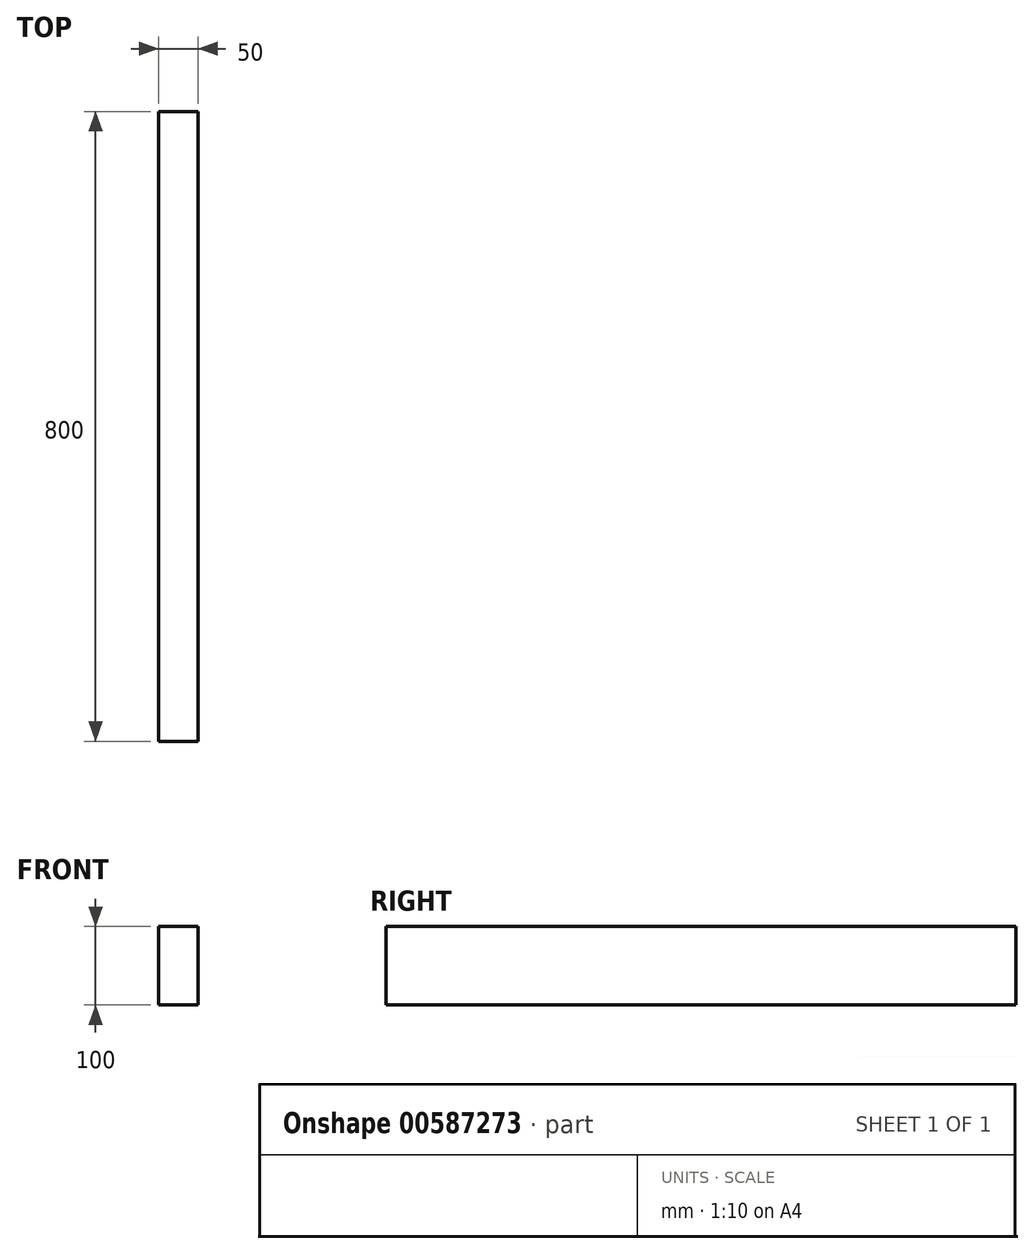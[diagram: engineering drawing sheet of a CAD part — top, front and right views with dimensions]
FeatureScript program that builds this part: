
annotation { "Feature Type Name" : "Feature", "Feature Type Description" : "" }
export const myFeature = defineFeature(function(context is Context, id is Id, definition is map)
    precondition{}
    {
        {
            var Q0;
            Q0=qCreatedBy(makeId("Front.planeOp"),FACE);
            var sketch = newSketch(context, id + "F0", { "sketchPlane" : qUnion([Q0])});
            skLineSegment(sketch, "E0.bottom", {"start": v(25, 50) * mm, "end": v(-25, 50) * mm});
            skLineSegment(sketch, "E0.top", {"start": v(25, -50) * mm, "end": v(-25, -50) * mm});
            skLineSegment(sketch, "E0.left", {"start": v(25, 50) * mm, "end": v(25, -50) * mm});
            skLineSegment(sketch, "E0.right", {"start": v(-25, 50) * mm, "end": v(-25, -50) * mm});
            skPoint(sketch, "E0.middle", {"position": v(0, 0) * mm});
            skSolve(sketch);
        }
        {
            var Q0;
            Q0=makeQuery(id+"F0.imprint","IMPRINT",FACE,{"disambiguationData":[TD([[makeQuery(id+"F0.imprint","IMPRINT",EDGE,{"derivedFrom":sQuery(id+"F0.wireOp",EDGE,"E0.bottom")}),1.0]])]});
            extrude(context, id + "F1", {"entities" : qUnion([Q0]), "endBound" : BoundingType.SYMMETRIC, "depth" : 800 * mm, "offsetDistance" : 25.4 * mm});
        }
    });
